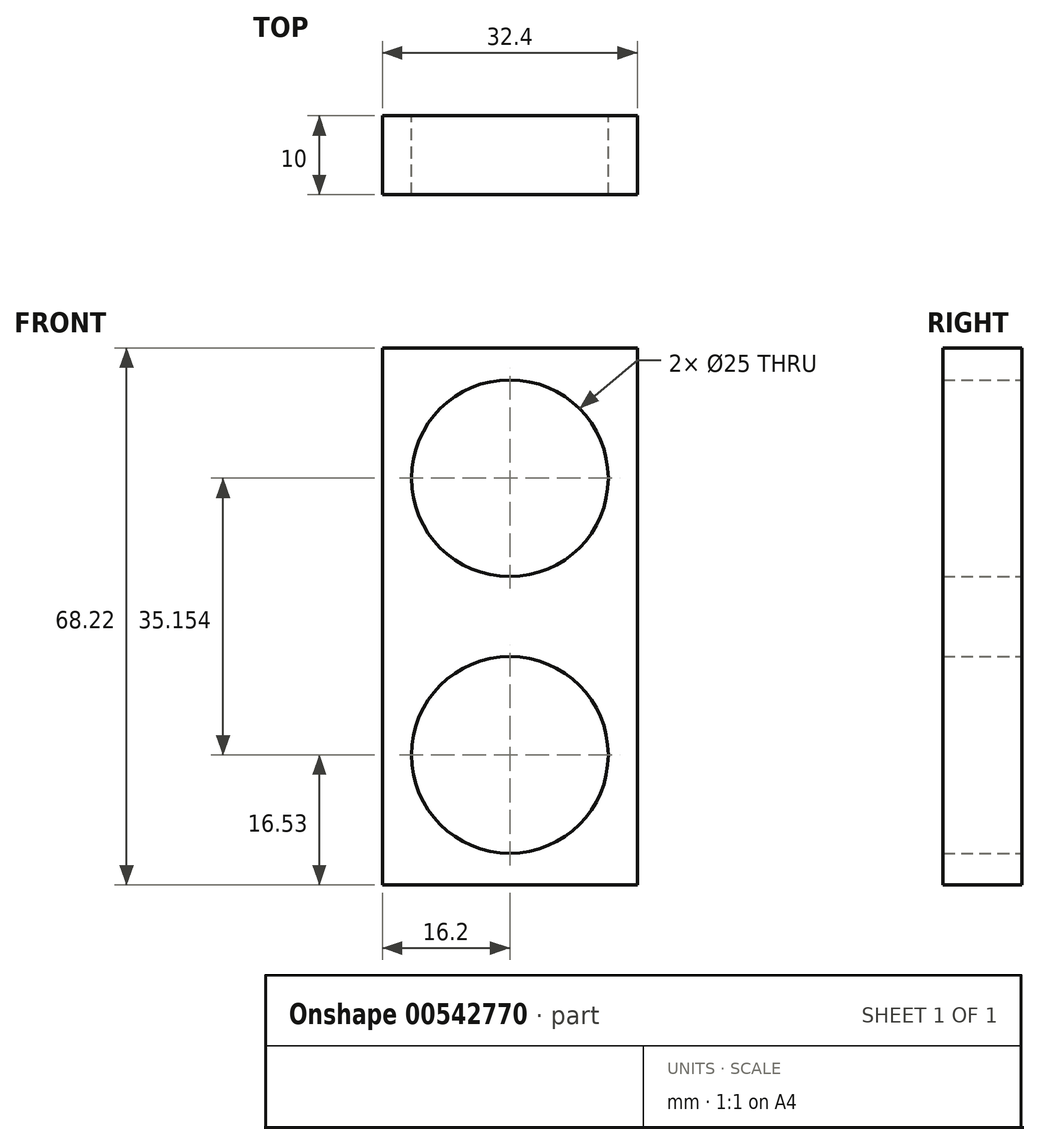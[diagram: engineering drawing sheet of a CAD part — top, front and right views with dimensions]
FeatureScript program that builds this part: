
annotation { "Feature Type Name" : "Feature", "Feature Type Description" : "" }
export const myFeature = defineFeature(function(context is Context, id is Id, definition is map)
    precondition{}
    {
        {
            var Q0;
            Q0=qCreatedBy(makeId("Front.planeOp"),FACE);
            var sketch = newSketch(context, id + "F0", { "sketchPlane" : qUnion([Q0])});
            skCircle(sketch, "E0", {"center": v(0, 0) * mm, "radius": 12.5 * mm});
            skCircle(sketch, "E1", {"center": v(0, 35.15) * mm, "radius": 12.5 * mm});
            skLineSegment(sketch, "E2", {"start": v(0, 35.15) * mm, "end": v(0, 0) * mm, "construction": true});
            skLineSegment(sketch, "E3.bottom", {"start": v(-16.2, 51.69) * mm, "end": v(16.2, 51.69) * mm});
            skLineSegment(sketch, "E3.top", {"start": v(-16.2, -16.53) * mm, "end": v(16.2, -16.53) * mm});
            skLineSegment(sketch, "E3.left", {"start": v(-16.2, 51.69) * mm, "end": v(-16.2, -16.53) * mm});
            skLineSegment(sketch, "E3.right", {"start": v(16.2, 51.69) * mm, "end": v(16.2, -16.53) * mm});
            skPoint(sketch, "E3.middle", {"position": v(0, 17.58) * mm});
            skSolve(sketch);
        }
        {
            var Q0;
            Q0 = qSketchRegion(id + "F0", true);
            extrude(context, id + "F1", {"entities" : qUnion([Q0]), "endBound" : BoundingType.SYMMETRIC, "depth" : 10 * mm, "offsetDistance" : 25 * mm});
        }
    });
